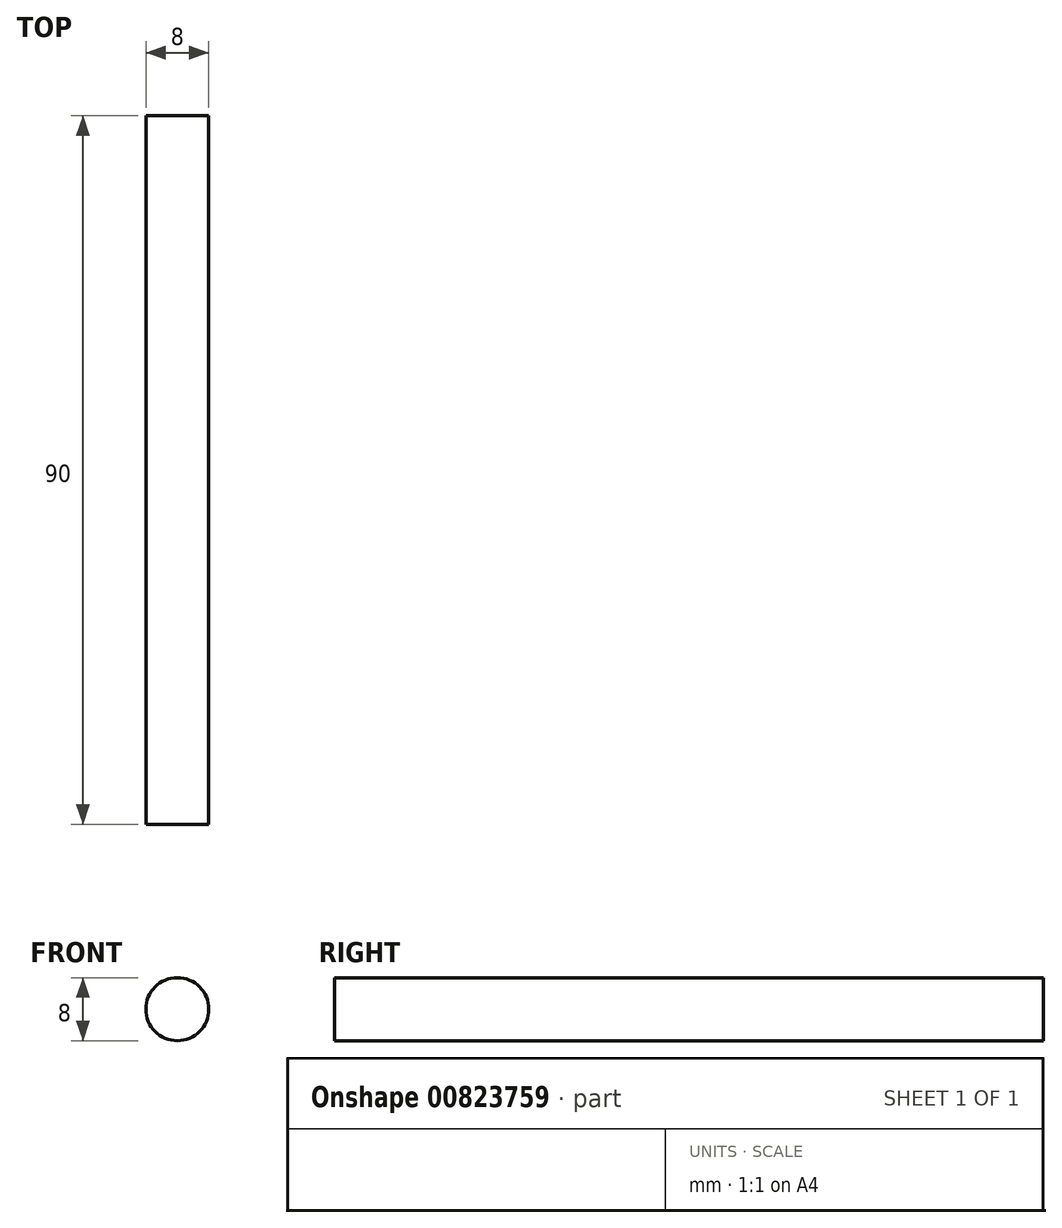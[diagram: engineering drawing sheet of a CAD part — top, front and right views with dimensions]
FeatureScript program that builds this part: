
annotation { "Feature Type Name" : "Feature", "Feature Type Description" : "" }
export const myFeature = defineFeature(function(context is Context, id is Id, definition is map)
    precondition{}
    {
        {
            var Q0;
            Q0=qCreatedBy(makeId("Front.planeOp"),FACE);
            var sketch = newSketch(context, id + "F0", { "sketchPlane" : qUnion([Q0])});
            skCircle(sketch, "E0", {"center": v(0, 0) * mm, "radius": 4 * mm});
            skSolve(sketch);
        }
        {
            var Q0;
            Q0=qSketchRegion(id+"F0",true);
            extrude(context, id + "F1", {"entities" : qUnion([Q0]), "depth" : 90 * mm, "offsetDistance" : 25 * mm});
        }
    });
